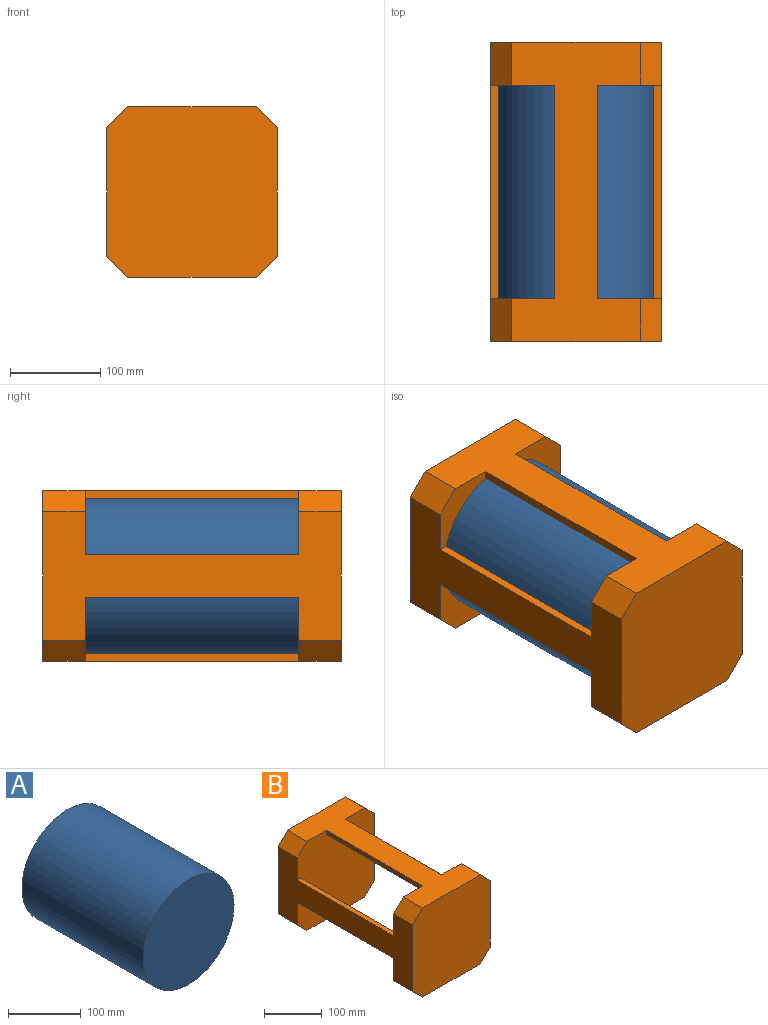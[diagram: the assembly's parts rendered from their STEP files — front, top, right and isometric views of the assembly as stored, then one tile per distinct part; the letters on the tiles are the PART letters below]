
ASSEMBLY  parts=2 mates=1
PART A: 3 faces, bbox 176.9x235.9x176.9 mm
  f0: cylinder r=88.45mm len=235.86mm, axis (0,-1,0), area 131071.8mm2, adj f1,f2
  f1: plane 176.89x176.89mm, normal (0,1,0), area 24576mm2, adj f0
  f2: plane 176.89x176.89mm, normal (0,-1,0), area 24576mm2, adj f0
PART B: 28 faces, bbox 188.7x330.2x188.7 mm
  f0: plane 188.69x188.69mm, normal (0,1,0), area 33177.2mm2, adj f1,f2,f3,f4,f5,f6,f7,f8
  f1: plane 330.2x141.51mm, normal (0,0,-1), area 24476.6mm2, adj f0,f2,f8,f9,f13,f14,f22,f23
  f2: plane 47.17x23.59mm, normal (0.71,0,-0.71), area 1573.4mm2, adj f0,f1,f3,f9
  f3: plane 330.2x141.51mm, normal (1,0,0), area 24476.6mm2, adj f0,f2,f4,f9,f19,f21,f22,f23
  f4: plane 47.17x23.59mm, normal (0.71,0,0.71), area 1573.4mm2, adj f0,f3,f5,f9
  f5: plane 330.2x141.51mm, normal (0,0,1), area 24476.6mm2, adj f0,f4,f6,f9,f10,f12,f22,f24
  f6: plane 47.17x23.59mm, normal (-0.71,0,0.71), area 1573.4mm2, adj f0,f5,f7,f9
  f7: plane 330.2x141.51mm, normal (-1,0,0), area 24476.6mm2, adj f0,f6,f8,f9,f17,f18,f22,f25
  f8: plane 47.17x23.59mm, normal (-0.71,0,-0.71), area 1573.4mm2, adj f0,f1,f7,f9
  f9: plane 188.69x188.69mm, normal (0,-1,0), area 34489.7mm2, adj f1,f2,f3,f4,f5,f6,f7,f8
  f10: plane 235.86x9.1mm, normal (-1,0,0), area 2146.1mm2, adj f0,f5,f11,f22
  f11: cylinder r=88.45mm len=235.86mm, axis (0,-1,0), area 11262mm2, adj f0,f10,f12,f22
  f12: plane 235.86x9.1mm, normal (1,0,0), area 2146.1mm2, adj f0,f5,f11,f22
  f13: plane 235.86x9.1mm, normal (-1,0,0), area 2146.1mm2, adj f0,f1,f15,f22
  f14: plane 235.86x9.1mm, normal (1,0,0), area 2146.1mm2, adj f0,f1,f15,f22
  f15: cylinder r=88.45mm len=235.86mm, axis (0,-1,0), area 11262mm2, adj f0,f13,f14,f22
  f16: cylinder r=88.45mm len=235.86mm, axis (0,-1,0), area 11262mm2, adj f0,f17,f18,f22
  f17: plane 235.86x9.1mm, normal (0,0,1), area 2146.1mm2, adj f0,f7,f16,f22
  f18: plane 235.86x9.1mm, normal (0,0,-1), area 2146.1mm2, adj f0,f7,f16,f22
  f19: plane 235.86x9.1mm, normal (0,0,1), area 2146.1mm2, adj f0,f3,f20,f22
  f20: cylinder r=88.45mm len=235.86mm, axis (0,-1,0), area 11262mm2, adj f0,f19,f21,f22
  f21: plane 235.86x9.1mm, normal (0,0,-1), area 2146.1mm2, adj f0,f3,f20,f22
  f22: plane 188.69x188.69mm, normal (0,-1,0), area 33177.2mm2, adj f1,f3,f5,f7,f10,f11,f12,f13
  f23: plane 47.17x23.59mm, normal (0.71,0,-0.71), area 1573.4mm2, adj f1,f3,f22,f27
  f24: plane 47.17x23.59mm, normal (0.71,0,0.71), area 1573.4mm2, adj f3,f5,f22,f27
  f25: plane 47.17x23.59mm, normal (-0.71,0,0.71), area 1573.4mm2, adj f5,f7,f22,f27
  f26: plane 47.17x23.59mm, normal (-0.71,0,-0.71), area 1573.4mm2, adj f1,f7,f22,f27
  f27: plane 188.69x188.69mm, normal (0,1,0), area 34489.7mm2, adj f1,f3,f5,f7,f23,f24,f25,f26
PLACE A t=(-523.45,-383.62,-3.75)mm
PLACE B t=(-0.21,-383.62,-3.75)mm
MATE fastened A.f0 <-> B.f20  axis (0,-1,0) through (-0.21,106.24,-3.75)mm
